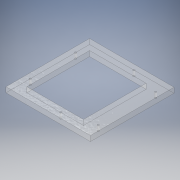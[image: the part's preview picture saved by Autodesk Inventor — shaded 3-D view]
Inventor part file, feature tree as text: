
AUTODESK INVENTOR PART (.ipt)
format: ipt  version: 2019 (Build 230136000, 136)  size: 137,216 bytes
history: native  units: mm
features: extrude x1, sketch x1
ambient origin geometry x8: Origin, YZ Plane, XZ Plane, XY Plane, X Axis, Y Axis, Z Axis, Center Point
bodies: Solid1 (feature_tree)
feature tree (2):
  extrude  "Extrusion1"  Depth=12.0mm
  sketch  "Sketch1"  dims[d15=6.0mm d16=0.0mm d22=12.0mm d23=12.0mm d24=12.0mm d25=20.0mm d26=65.0mm d28=2.1mm d30=3.0mm d31=72.0mm d32=6.0mm d33=6.0mm d34=6.0mm d35=20.0mm d36=10.0mm]
